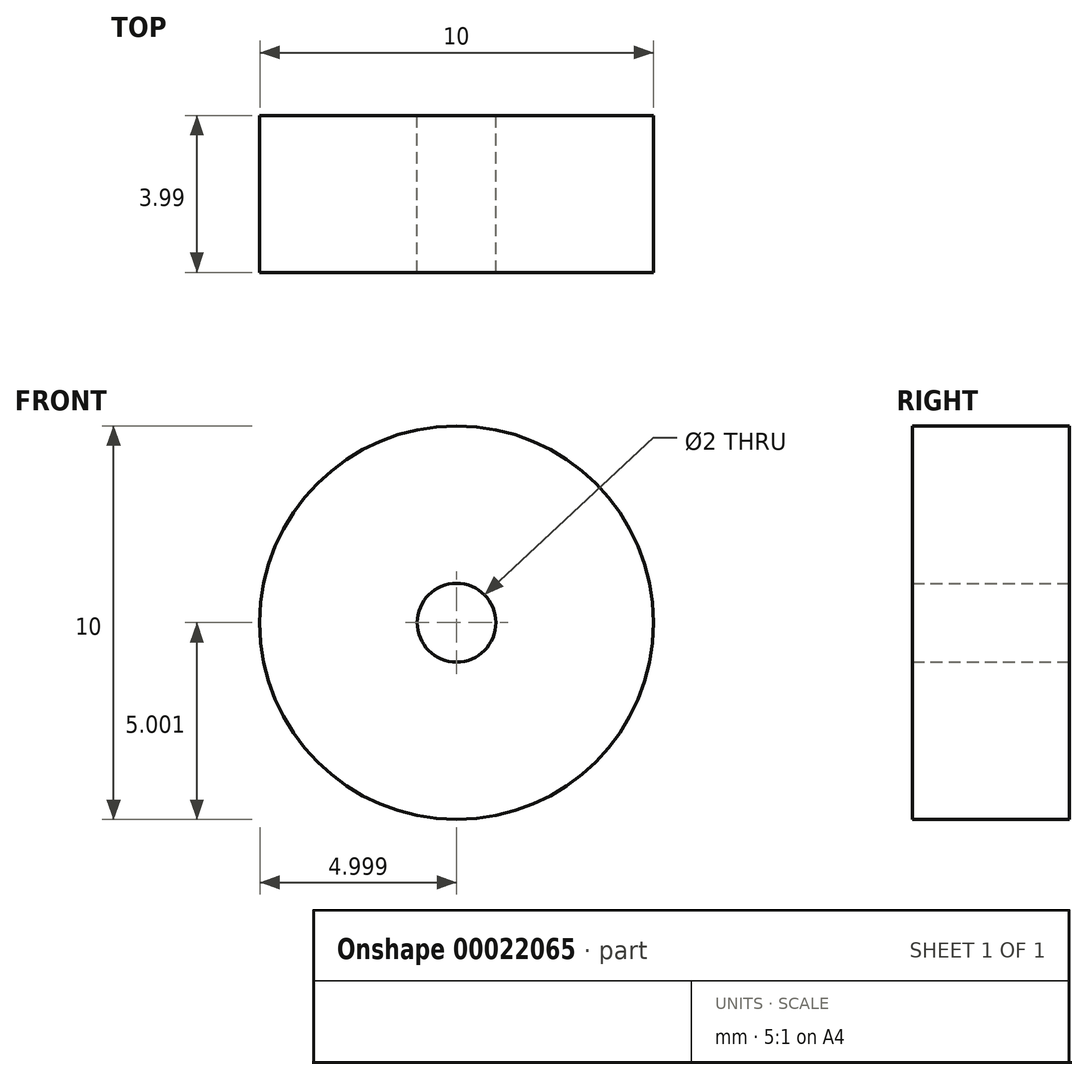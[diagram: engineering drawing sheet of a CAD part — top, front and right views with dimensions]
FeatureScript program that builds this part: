
annotation { "Feature Type Name" : "Feature", "Feature Type Description" : "" }
export const myFeature = defineFeature(function(context is Context, id is Id, definition is map)
    precondition{}
    {
        {
            var Q0;
            Q0=qCreatedBy(makeId("Front.planeOp"),FACE);
            var sketch = newSketch(context, id + "F0", { "sketchPlane" : qUnion([Q0])});
            skCircle(sketch, "E0", {"center": v(-390.96, 4.66) * mm, "radius": 5 * mm});
            skCircle(sketch, "E1", {"center": v(-390.96, 4.66) * mm, "radius": 1 * mm});
            skSolve(sketch);
        }
        {
            var Q0;
            Q0=makeQuery(id+"F0.imprint","IMPRINT",FACE,{"disambiguationData":[TD([[makeQuery(id+"F0.imprint","IMPRINT",EDGE,{"derivedFrom":sQuery(id+"F0.wireOp",EDGE,"E0")}),1.0]])]});
            extrude(context, id + "F1", {"entities" : qUnion([Q0]), "depth" : 4 * mm});
        }
    });
